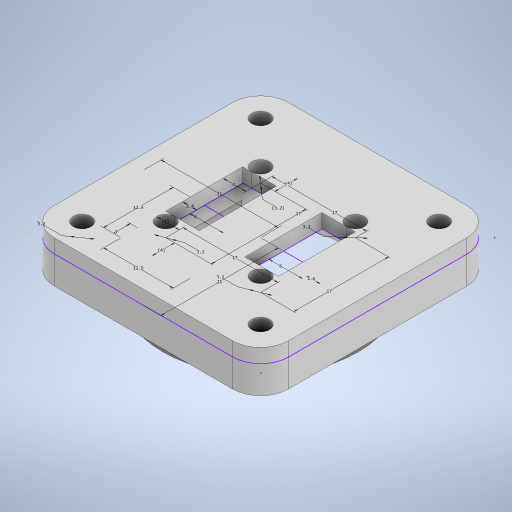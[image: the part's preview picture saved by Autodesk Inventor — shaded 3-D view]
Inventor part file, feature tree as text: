
AUTODESK INVENTOR PART (.ipt)
format: ipt  version: 2024 (Build 280153000, 153)  size: 336,384 bytes
history: native  units: mm
features: extrude x3, sketch x2, other x1
ambient origin geometry x8: Origin, YZ Plane, XZ Plane, XY Plane, X Axis, Y Axis, Z Axis, Center Point
bodies: Body1 (feature_tree)
feature tree (6):
  other  "ソリッド1"
  sketch  "スケッチ1"
  extrude  "押し出し2"  Depth=21.0mm
  sketch  "スケッチ2"
  extrude  "押し出し4"  Depth=21.0mm
  extrude  "押し出し5"  Depth=3.2mm
